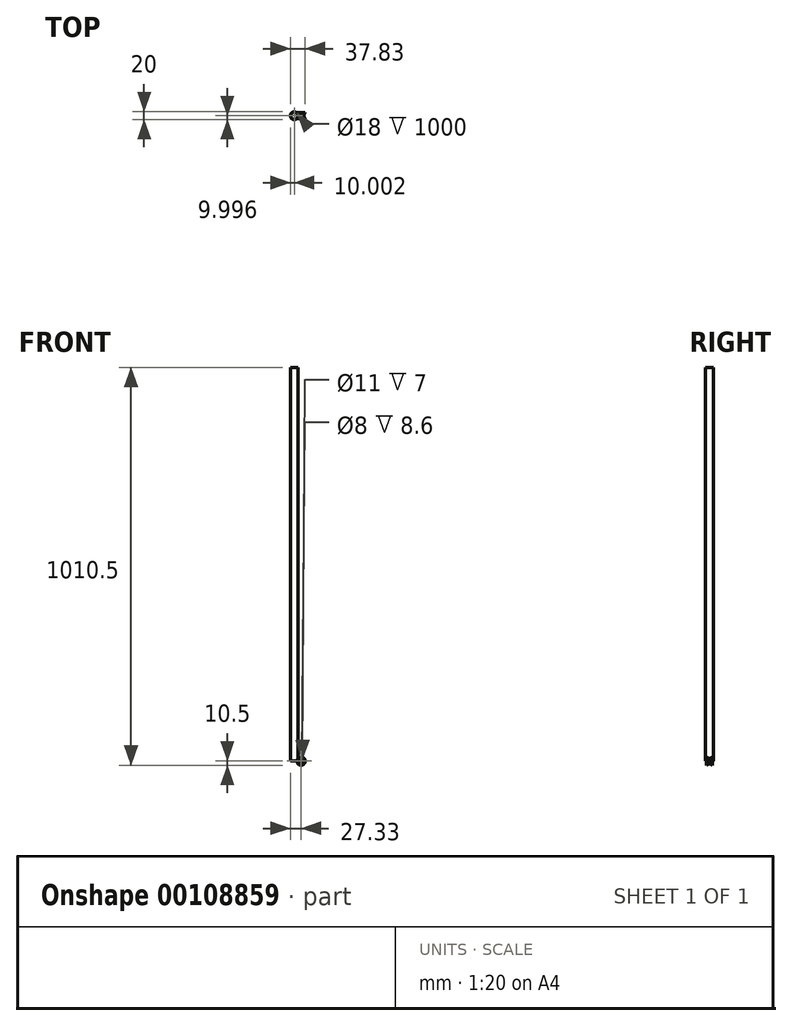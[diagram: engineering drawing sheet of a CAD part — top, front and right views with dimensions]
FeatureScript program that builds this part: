
annotation { "Feature Type Name" : "Feature", "Feature Type Description" : "" }
export const myFeature = defineFeature(function(context is Context, id is Id, definition is map)
    precondition{}
    {
        {
            var Q0;
            Q0=qCreatedBy(makeId("Top.planeOp"),FACE);
            var sketch = newSketch(context, id + "F0", { "sketchPlane" : qUnion([Q0])});
            skLineSegment(sketch, "E0", {"start": v(-4, 10.48) * mm, "end": v(-4, 1.88) * mm});
            skLineSegment(sketch, "E1", {"start": v(-4, 1.88) * mm, "end": v(-5.5, 1.88) * mm});
            skLineSegment(sketch, "E2", {"start": v(-5.5, 1.88) * mm, "end": v(-5.5, -5.12) * mm});
            skLineSegment(sketch, "E3", {"start": v(-4, 10.48) * mm, "end": v(-10.5, 10.48) * mm});
            skArc(sketch, "E4", {"start": v(-10.5, -4.62) * mm, "mid": v(-8.22, -1.44) * mm, "end": v(-7.34, 2.38) * mm});
            skLineSegment(sketch, "E5", {"start": v(0, 17.53) * mm, "end": v(0, -13.51) * mm, "construction": true});
            skLineSegment(sketch, "E6", {"start": v(-10.5, -4.62) * mm, "end": v(-10.5, -5.12) * mm});
            skLineSegment(sketch, "E7", {"start": v(-10.5, -5.12) * mm, "end": v(-5.5, -5.12) * mm});
            skLineSegment(sketch, "E8", {"start": v(-10.5, 10.48) * mm, "end": v(-10.5, 9.98) * mm});
            skLineSegment(sketch, "E9", {"start": v(-17.33, 2.68) * mm, "end": v(17.92, 2.68) * mm, "construction": true});
            skLineSegment(sketch, "E10", {"start": v(-7.33, 2.86) * mm, "end": v(-7.18, -5.8) * mm, "construction": true});
            skPoint(sketch, "E11", {"position": v(-7.33, 2.86) * mm});
            skLineSegment(sketch, "E12", {"start": v(-17.33, -9.23) * mm, "end": v(-17.33, 18.38) * mm, "construction": true});
            skLineSegment(sketch, "E13", {"start": v(-7.34, 2.38) * mm, "end": v(-7.24, 2.38) * mm});
            skLineSegment(sketch, "E14", {"start": v(-7.24, 2.38) * mm, "end": v(-7.24, 2.98) * mm});
            skLineSegment(sketch, "E15", {"start": v(-7.24, 2.98) * mm, "end": v(-7.34, 2.98) * mm});
            skArc(sketch, "E16.trimOffspring", {"start": v(-7.34, 2.98) * mm, "mid": v(-8.22, 6.8) * mm, "end": v(-10.5, 9.98) * mm});
            skSolve(sketch);
        }
        {
            var Q0;
            Q0=makeQuery(id+"F0.imprint","IMPRINT",FACE,{"disambiguationData":[TD([[makeQuery(id+"F0.imprint","IMPRINT",EDGE,{"derivedFrom":sQuery(id+"F0.wireOp",EDGE,"E0")}),-1.0]])]});
            var Q1;
            Q1=sQuery(id+"F0.wireOp",EDGE,"E5");
            revolve(context, id + "F1", {"entities" : qUnion([Q0]), "axis" : qUnion([Q1]), "revolveType" : RevolveType.FULL});
        }
        {
            var Q0;
            Q0=qCreatedBy(makeId("Top.planeOp"),FACE);
            var sketch = newSketch(context, id + "F2", { "sketchPlane" : qUnion([Q0])});
            skPoint(sketch, "E17", {"position": v(-7.32, 2.82) * mm});
            skCircle(sketch, "E18", {"center": v(-17.33, 2.82) * mm, "radius": 10 * mm});
            skCircle(sketch, "E19", {"center": v(-17.33, 2.82) * mm, "radius": 9 * mm});
            skLineSegment(sketch, "E20", {"start": v(-17.4, 12.82) * mm, "end": v(1.83, 12.95) * mm, "construction": true});
            skSolve(sketch);
        }
        {
            var Q0;
            Q0 = qSketchRegion(id + "F2", true);
            extrude(context, id + "F3", {"entities" : qUnion([Q0]), "depth" : 1000 * mm});
        }
    });
